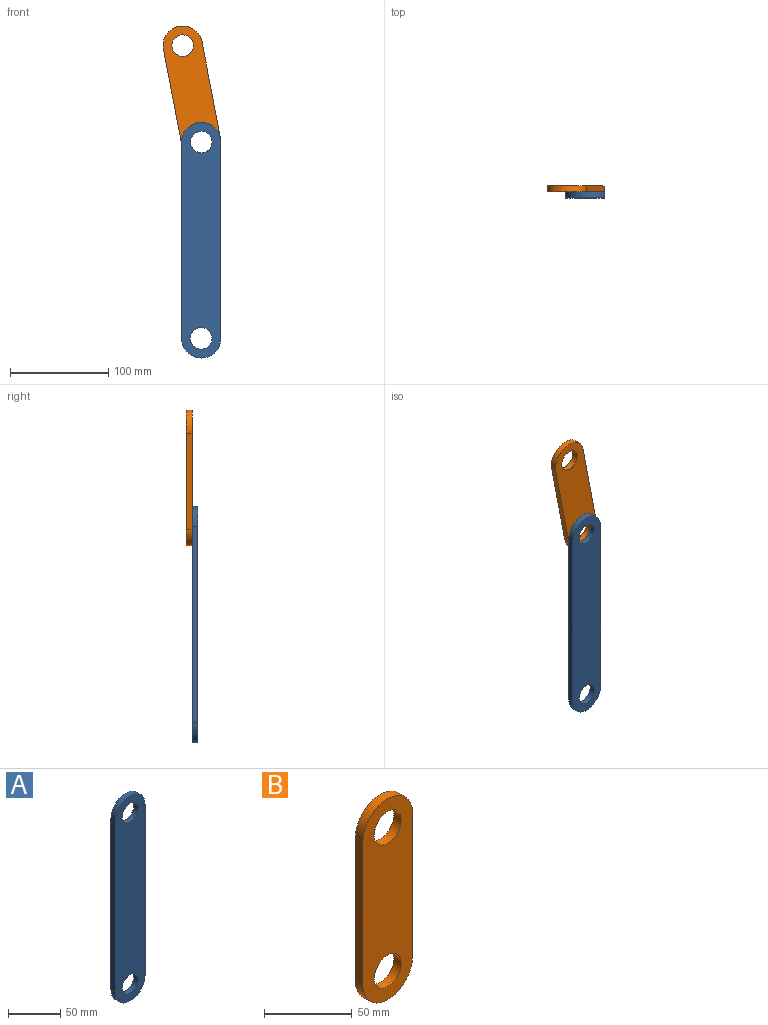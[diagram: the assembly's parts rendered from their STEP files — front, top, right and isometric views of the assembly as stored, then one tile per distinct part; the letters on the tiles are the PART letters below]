
ASSEMBLY  parts=2 mates=1
PART A: 8 faces, bbox 40x6x240 mm
  f0: plane 200x6mm, normal (1,0,0), area 1200mm2, adj f4,f5,f6,f7
  f1: cylinder r=11mm len=22mm, axis (0,1,0), area 414.7mm2, adj f4,f5
  f2: cylinder r=11mm len=22mm, axis (0,1,0), area 414.7mm2, adj f4,f5
  f3: plane 200x6mm, normal (-1,0,0), area 1200mm2, adj f4,f5,f6,f7
  f4: plane 240x40mm, normal (0,-1,0), area 8496.4mm2, adj f0,f1,f2,f3,f6,f7
  f5: plane 240x40mm, normal (0,1,0), area 8496.4mm2, adj f0,f1,f2,f3,f6,f7
  f6: cylinder r=20mm len=40mm, axis (0,-1,0), area 377mm2, adj f0,f3,f4,f5
  f7: cylinder r=20mm len=40mm, axis (0,1,0), area 377mm2, adj f0,f3,f4,f5
PART B: 8 faces, bbox 40x6x140 mm
  f0: plane 100x6mm, normal (1,0,0), area 600mm2, adj f4,f5,f6,f7
  f1: cylinder r=11mm len=22mm, axis (0,1,0), area 414.7mm2, adj f4,f5
  f2: cylinder r=11mm len=22mm, axis (0,1,0), area 414.7mm2, adj f4,f5
  f3: plane 100x6mm, normal (-1,0,0), area 600mm2, adj f4,f5,f6,f7
  f4: plane 140x40mm, normal (0,-1,0), area 4496.4mm2, adj f0,f1,f2,f3,f6,f7
  f5: plane 140x40mm, normal (0,1,0), area 4496.4mm2, adj f0,f1,f2,f3,f6,f7
  f6: cylinder r=20mm len=40mm, axis (0,-1,0), area 377mm2, adj f0,f3,f4,f5
  f7: cylinder r=20mm len=40mm, axis (0,1,0), area 377mm2, adj f0,f3,f4,f5
PLACE A t=(-5.73,-88.97,92.51)mm fixed
PLACE B rot(axis=(0,1,0),169.1deg) t=(-5.73,-82.97,92.51)mm
MATE revolute B.f7 <-> A.f7  axis (0,-1,0) through (-5.73,-88.97,92.51)mm
